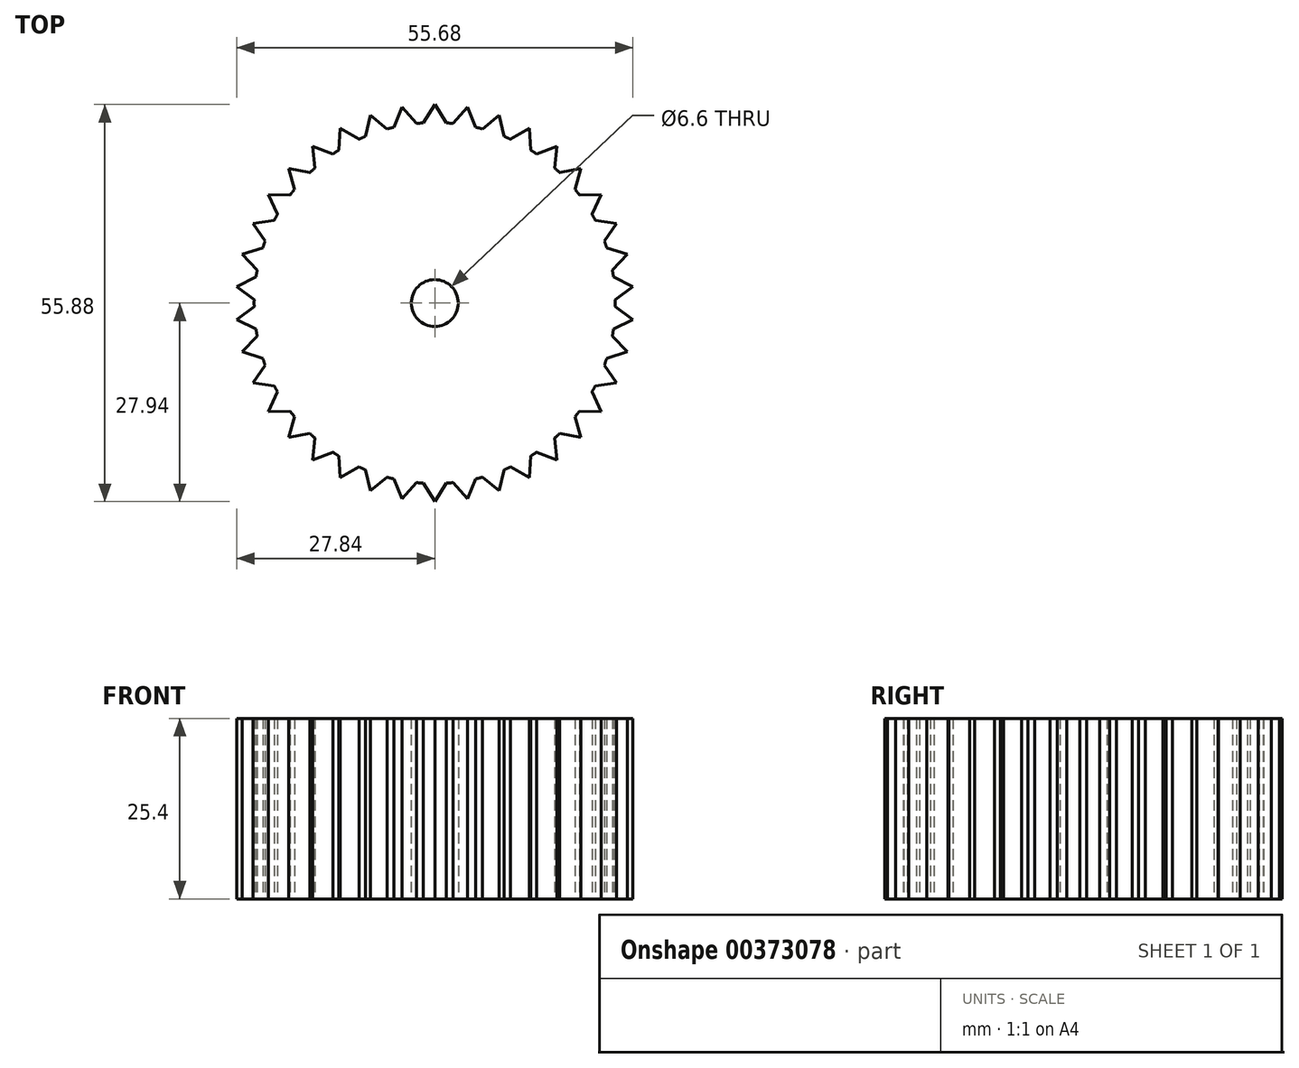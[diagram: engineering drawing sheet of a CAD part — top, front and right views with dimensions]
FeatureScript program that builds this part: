
annotation { "Feature Type Name" : "Feature", "Feature Type Description" : "" }
export const myFeature = defineFeature(function(context is Context, id is Id, definition is map)
    precondition{}
    {
        {
            var Q0;
            Q0=qCreatedBy(makeId("Top.planeOp"),FACE);
            var sketch = newSketch(context, id + "F0", { "sketchPlane" : qUnion([Q0])});
            skCircle(sketch, "E0", {"center": v(0, 0) * mm, "radius": 25.4 * mm});
            skCircle(sketch, "E1", {"center": v(0, 0) * mm, "radius": 3.3 * mm});
            skLineSegment(sketch, "E2", {"start": v(0, 25.4) * mm, "end": v(0, 27.94) * mm});
            skLineSegment(sketch, "E3", {"start": v(0, 27.94) * mm, "end": v(1.6, 25.35) * mm});
            skLineSegment(sketch, "E4", {"start": v(0, 27.94) * mm, "end": v(-1.6, 25.35) * mm});
            skLineSegment(sketch, "E5.1.0", {"start": v(-4.6, 27.56) * mm, "end": v(-5.76, 24.74) * mm});
            skLineSegment(sketch, "E5.1.1", {"start": v(-4.6, 27.56) * mm, "end": v(-2.59, 25.27) * mm});
            skLineSegment(sketch, "E5.1.2", {"start": v(-4.18, 25.05) * mm, "end": v(-4.6, 27.56) * mm});
            skLineSegment(sketch, "E5.2.0", {"start": v(-9.07, 26.43) * mm, "end": v(-9.75, 23.45) * mm});
            skLineSegment(sketch, "E5.2.1", {"start": v(-9.07, 26.43) * mm, "end": v(-6.71, 24.5) * mm});
            skLineSegment(sketch, "E5.2.2", {"start": v(-8.25, 24.02) * mm, "end": v(-9.07, 26.43) * mm});
            skLineSegment(sketch, "E5.3.0", {"start": v(-13.3, 24.57) * mm, "end": v(-13.48, 21.53) * mm});
            skLineSegment(sketch, "E5.3.1", {"start": v(-13.3, 24.57) * mm, "end": v(-10.65, 23.06) * mm});
            skLineSegment(sketch, "E5.3.2", {"start": v(-12.09, 22.34) * mm, "end": v(-13.3, 24.57) * mm});
            skLineSegment(sketch, "E5.4.0", {"start": v(-17.16, 22.05) * mm, "end": v(-16.84, 19.02) * mm});
            skLineSegment(sketch, "E5.4.1", {"start": v(-17.16, 22.05) * mm, "end": v(-14.3, 21) * mm});
            skLineSegment(sketch, "E5.4.2", {"start": v(-15.6, 20.04) * mm, "end": v(-17.16, 22.05) * mm});
            skLineSegment(sketch, "E5.5.0", {"start": v(-20.56, 18.92) * mm, "end": v(-19.74, 15.99) * mm});
            skLineSegment(sketch, "E5.5.1", {"start": v(-20.56, 18.92) * mm, "end": v(-17.56, 18.35) * mm});
            skLineSegment(sketch, "E5.5.2", {"start": v(-18.69, 17.2) * mm, "end": v(-20.56, 18.92) * mm});
            skLineSegment(sketch, "E5.6.0", {"start": v(-23.4, 15.28) * mm, "end": v(-22.1, 12.52) * mm});
            skLineSegment(sketch, "E5.6.1", {"start": v(-23.4, 15.28) * mm, "end": v(-20.34, 15.2) * mm});
            skLineSegment(sketch, "E5.6.2", {"start": v(-21.26, 13.9) * mm, "end": v(-23.4, 15.28) * mm});
            skLineSegment(sketch, "E5.7.0", {"start": v(-25.59, 11.22) * mm, "end": v(-23.86, 8.71) * mm});
            skLineSegment(sketch, "E5.7.1", {"start": v(-25.59, 11.22) * mm, "end": v(-22.57, 11.65) * mm});
            skLineSegment(sketch, "E5.7.2", {"start": v(-23.26, 10.2) * mm, "end": v(-25.59, 11.22) * mm});
            skLineSegment(sketch, "E5.8.0", {"start": v(-27.09, 6.86) * mm, "end": v(-24.97, 4.67) * mm});
            skLineSegment(sketch, "E5.8.1", {"start": v(-27.09, 6.86) * mm, "end": v(-24.18, 7.78) * mm});
            skLineSegment(sketch, "E5.8.2", {"start": v(-24.62, 6.24) * mm, "end": v(-27.09, 6.86) * mm});
            skLineSegment(sketch, "E5.9.0", {"start": v(-27.84, 2.3) * mm, "end": v(-25.4, 0.5) * mm});
            skLineSegment(sketch, "E5.9.1", {"start": v(-27.84, 2.3) * mm, "end": v(-25.13, 3.7) * mm});
            skLineSegment(sketch, "E5.9.2", {"start": v(-25.31, 2.1) * mm, "end": v(-27.84, 2.3) * mm});
            skLineSegment(sketch, "E5.10.0", {"start": v(-27.84, -2.3) * mm, "end": v(-25.13, -3.7) * mm});
            skLineSegment(sketch, "E5.10.1", {"start": v(-27.84, -2.3) * mm, "end": v(-25.4, -0.5) * mm});
            skLineSegment(sketch, "E5.10.2", {"start": v(-25.31, -2.1) * mm, "end": v(-27.84, -2.3) * mm});
            skLineSegment(sketch, "E5.11.0", {"start": v(-27.09, -6.86) * mm, "end": v(-24.18, -7.78) * mm});
            skLineSegment(sketch, "E5.11.1", {"start": v(-27.09, -6.86) * mm, "end": v(-24.97, -4.67) * mm});
            skLineSegment(sketch, "E5.11.2", {"start": v(-24.62, -6.24) * mm, "end": v(-27.09, -6.86) * mm});
            skLineSegment(sketch, "E5.12.0", {"start": v(-25.59, -11.22) * mm, "end": v(-22.57, -11.65) * mm});
            skLineSegment(sketch, "E5.12.1", {"start": v(-25.59, -11.22) * mm, "end": v(-23.86, -8.71) * mm});
            skLineSegment(sketch, "E5.12.2", {"start": v(-23.26, -10.2) * mm, "end": v(-25.59, -11.22) * mm});
            skLineSegment(sketch, "E5.13.0", {"start": v(-23.4, -15.28) * mm, "end": v(-20.34, -15.2) * mm});
            skLineSegment(sketch, "E5.13.1", {"start": v(-23.4, -15.28) * mm, "end": v(-22.1, -12.52) * mm});
            skLineSegment(sketch, "E5.13.2", {"start": v(-21.26, -13.9) * mm, "end": v(-23.4, -15.28) * mm});
            skLineSegment(sketch, "E5.14.0", {"start": v(-20.56, -18.92) * mm, "end": v(-17.56, -18.35) * mm});
            skLineSegment(sketch, "E5.14.1", {"start": v(-20.56, -18.92) * mm, "end": v(-19.74, -15.99) * mm});
            skLineSegment(sketch, "E5.14.2", {"start": v(-18.69, -17.2) * mm, "end": v(-20.56, -18.92) * mm});
            skLineSegment(sketch, "E5.15.0", {"start": v(-17.16, -22.05) * mm, "end": v(-14.3, -21) * mm});
            skLineSegment(sketch, "E5.15.1", {"start": v(-17.16, -22.05) * mm, "end": v(-16.84, -19.02) * mm});
            skLineSegment(sketch, "E5.15.2", {"start": v(-15.6, -20.04) * mm, "end": v(-17.16, -22.05) * mm});
            skLineSegment(sketch, "E5.16.0", {"start": v(-13.3, -24.57) * mm, "end": v(-10.65, -23.06) * mm});
            skLineSegment(sketch, "E5.16.1", {"start": v(-13.3, -24.57) * mm, "end": v(-13.48, -21.53) * mm});
            skLineSegment(sketch, "E5.16.2", {"start": v(-12.09, -22.34) * mm, "end": v(-13.3, -24.57) * mm});
            skLineSegment(sketch, "E5.17.0", {"start": v(-9.07, -26.43) * mm, "end": v(-6.71, -24.5) * mm});
            skLineSegment(sketch, "E5.17.1", {"start": v(-9.07, -26.43) * mm, "end": v(-9.75, -23.45) * mm});
            skLineSegment(sketch, "E5.17.2", {"start": v(-8.25, -24.02) * mm, "end": v(-9.07, -26.43) * mm});
            skLineSegment(sketch, "E5.18.0", {"start": v(-4.6, -27.56) * mm, "end": v(-2.59, -25.27) * mm});
            skLineSegment(sketch, "E5.18.1", {"start": v(-4.6, -27.56) * mm, "end": v(-5.76, -24.74) * mm});
            skLineSegment(sketch, "E5.18.2", {"start": v(-4.18, -25.05) * mm, "end": v(-4.6, -27.56) * mm});
            skLineSegment(sketch, "E5.19.0", {"start": v(0, -27.94) * mm, "end": v(1.6, -25.35) * mm});
            skLineSegment(sketch, "E5.19.1", {"start": v(0, -27.94) * mm, "end": v(-1.6, -25.35) * mm});
            skLineSegment(sketch, "E5.19.2", {"start": v(0, -25.4) * mm, "end": v(0, -27.94) * mm});
            skLineSegment(sketch, "E5.20.0", {"start": v(4.6, -27.56) * mm, "end": v(5.76, -24.74) * mm});
            skLineSegment(sketch, "E5.20.1", {"start": v(4.6, -27.56) * mm, "end": v(2.59, -25.27) * mm});
            skLineSegment(sketch, "E5.20.2", {"start": v(4.18, -25.05) * mm, "end": v(4.6, -27.56) * mm});
            skLineSegment(sketch, "E5.21.0", {"start": v(9.07, -26.43) * mm, "end": v(9.75, -23.45) * mm});
            skLineSegment(sketch, "E5.21.1", {"start": v(9.07, -26.43) * mm, "end": v(6.71, -24.5) * mm});
            skLineSegment(sketch, "E5.21.2", {"start": v(8.25, -24.02) * mm, "end": v(9.07, -26.43) * mm});
            skLineSegment(sketch, "E5.22.0", {"start": v(13.3, -24.57) * mm, "end": v(13.48, -21.53) * mm});
            skLineSegment(sketch, "E5.22.1", {"start": v(13.3, -24.57) * mm, "end": v(10.65, -23.06) * mm});
            skLineSegment(sketch, "E5.22.2", {"start": v(12.09, -22.34) * mm, "end": v(13.3, -24.57) * mm});
            skLineSegment(sketch, "E5.23.0", {"start": v(17.16, -22.05) * mm, "end": v(16.84, -19.02) * mm});
            skLineSegment(sketch, "E5.23.1", {"start": v(17.16, -22.05) * mm, "end": v(14.3, -21) * mm});
            skLineSegment(sketch, "E5.23.2", {"start": v(15.6, -20.04) * mm, "end": v(17.16, -22.05) * mm});
            skLineSegment(sketch, "E5.24.0", {"start": v(20.56, -18.92) * mm, "end": v(19.74, -15.99) * mm});
            skLineSegment(sketch, "E5.24.1", {"start": v(20.56, -18.92) * mm, "end": v(17.56, -18.35) * mm});
            skLineSegment(sketch, "E5.24.2", {"start": v(18.69, -17.2) * mm, "end": v(20.56, -18.92) * mm});
            skLineSegment(sketch, "E5.25.0", {"start": v(23.4, -15.28) * mm, "end": v(22.1, -12.52) * mm});
            skLineSegment(sketch, "E5.25.1", {"start": v(23.4, -15.28) * mm, "end": v(20.34, -15.2) * mm});
            skLineSegment(sketch, "E5.25.2", {"start": v(21.26, -13.9) * mm, "end": v(23.4, -15.28) * mm});
            skLineSegment(sketch, "E5.26.0", {"start": v(25.59, -11.22) * mm, "end": v(23.86, -8.71) * mm});
            skLineSegment(sketch, "E5.26.1", {"start": v(25.59, -11.22) * mm, "end": v(22.57, -11.65) * mm});
            skLineSegment(sketch, "E5.26.2", {"start": v(23.26, -10.2) * mm, "end": v(25.59, -11.22) * mm});
            skLineSegment(sketch, "E5.27.0", {"start": v(27.09, -6.86) * mm, "end": v(24.97, -4.67) * mm});
            skLineSegment(sketch, "E5.27.1", {"start": v(27.09, -6.86) * mm, "end": v(24.18, -7.78) * mm});
            skLineSegment(sketch, "E5.27.2", {"start": v(24.62, -6.24) * mm, "end": v(27.09, -6.86) * mm});
            skLineSegment(sketch, "E5.28.0", {"start": v(27.84, -2.3) * mm, "end": v(25.4, -0.5) * mm});
            skLineSegment(sketch, "E5.28.1", {"start": v(27.84, -2.3) * mm, "end": v(25.13, -3.7) * mm});
            skLineSegment(sketch, "E5.28.2", {"start": v(25.31, -2.1) * mm, "end": v(27.84, -2.3) * mm});
            skLineSegment(sketch, "E5.29.0", {"start": v(27.84, 2.3) * mm, "end": v(25.13, 3.7) * mm});
            skLineSegment(sketch, "E5.29.1", {"start": v(27.84, 2.3) * mm, "end": v(25.4, 0.5) * mm});
            skLineSegment(sketch, "E5.29.2", {"start": v(25.31, 2.1) * mm, "end": v(27.84, 2.3) * mm});
            skLineSegment(sketch, "E5.30.0", {"start": v(27.09, 6.86) * mm, "end": v(24.18, 7.78) * mm});
            skLineSegment(sketch, "E5.30.1", {"start": v(27.09, 6.86) * mm, "end": v(24.97, 4.67) * mm});
            skLineSegment(sketch, "E5.30.2", {"start": v(24.62, 6.24) * mm, "end": v(27.09, 6.86) * mm});
            skLineSegment(sketch, "E5.31.0", {"start": v(25.59, 11.22) * mm, "end": v(22.57, 11.65) * mm});
            skLineSegment(sketch, "E5.31.1", {"start": v(25.59, 11.22) * mm, "end": v(23.86, 8.71) * mm});
            skLineSegment(sketch, "E5.31.2", {"start": v(23.26, 10.2) * mm, "end": v(25.59, 11.22) * mm});
            skLineSegment(sketch, "E5.32.0", {"start": v(23.4, 15.28) * mm, "end": v(20.34, 15.2) * mm});
            skLineSegment(sketch, "E5.32.1", {"start": v(23.4, 15.28) * mm, "end": v(22.1, 12.52) * mm});
            skLineSegment(sketch, "E5.32.2", {"start": v(21.26, 13.9) * mm, "end": v(23.4, 15.28) * mm});
            skLineSegment(sketch, "E5.33.0", {"start": v(20.56, 18.92) * mm, "end": v(17.56, 18.35) * mm});
            skLineSegment(sketch, "E5.33.1", {"start": v(20.56, 18.92) * mm, "end": v(19.74, 15.99) * mm});
            skLineSegment(sketch, "E5.33.2", {"start": v(18.69, 17.2) * mm, "end": v(20.56, 18.92) * mm});
            skLineSegment(sketch, "E5.34.0", {"start": v(17.16, 22.05) * mm, "end": v(14.3, 21) * mm});
            skLineSegment(sketch, "E5.34.1", {"start": v(17.16, 22.05) * mm, "end": v(16.84, 19.02) * mm});
            skLineSegment(sketch, "E5.34.2", {"start": v(15.6, 20.04) * mm, "end": v(17.16, 22.05) * mm});
            skLineSegment(sketch, "E5.35.0", {"start": v(13.3, 24.57) * mm, "end": v(10.65, 23.06) * mm});
            skLineSegment(sketch, "E5.35.1", {"start": v(13.3, 24.57) * mm, "end": v(13.48, 21.53) * mm});
            skLineSegment(sketch, "E5.35.2", {"start": v(12.09, 22.34) * mm, "end": v(13.3, 24.57) * mm});
            skLineSegment(sketch, "E5.36.0", {"start": v(9.07, 26.43) * mm, "end": v(6.71, 24.5) * mm});
            skLineSegment(sketch, "E5.36.1", {"start": v(9.07, 26.43) * mm, "end": v(9.75, 23.45) * mm});
            skLineSegment(sketch, "E5.36.2", {"start": v(8.25, 24.02) * mm, "end": v(9.07, 26.43) * mm});
            skLineSegment(sketch, "E5.37.0", {"start": v(4.6, 27.56) * mm, "end": v(2.59, 25.27) * mm});
            skLineSegment(sketch, "E5.37.1", {"start": v(4.6, 27.56) * mm, "end": v(5.76, 24.74) * mm});
            skLineSegment(sketch, "E5.37.2", {"start": v(4.18, 25.05) * mm, "end": v(4.6, 27.56) * mm});
            skSolve(sketch);
        }
        {
            var Q0;
            Q0 = qSketchRegion(id + "F0", true);
            extrude(context, id + "F1", {"entities" : qUnion([Q0]), "depth" : 25.4 * mm});
        }
    });
